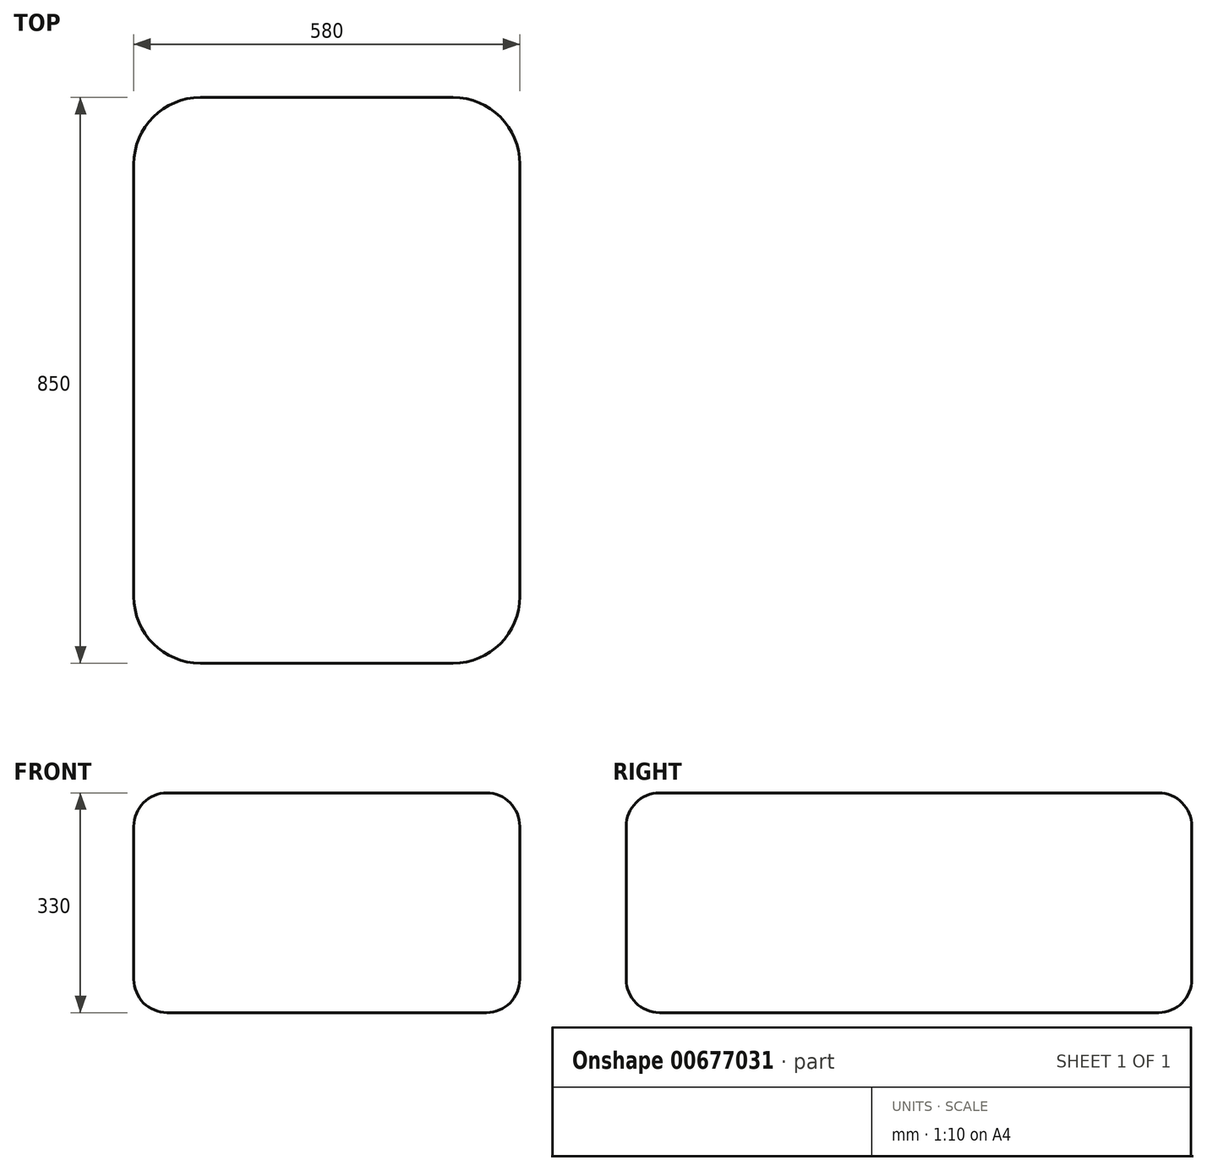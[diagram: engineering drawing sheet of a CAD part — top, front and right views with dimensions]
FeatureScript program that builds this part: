
annotation { "Feature Type Name" : "Feature", "Feature Type Description" : "" }
export const myFeature = defineFeature(function(context is Context, id is Id, definition is map)
    precondition{}
    {
        {
            var Q0;
            Q0=qCreatedBy(makeId("Top.planeOp"),FACE);
            var sketch = newSketch(context, id + "F0", { "sketchPlane" : qUnion([Q0])});
            skLineSegment(sketch, "E0.bottom", {"start": v(0, 0) * mm, "end": v(580, 0) * mm});
            skLineSegment(sketch, "E0.top", {"start": v(0, -850) * mm, "end": v(580, -850) * mm});
            skLineSegment(sketch, "E0.left", {"start": v(0, 0) * mm, "end": v(0, -850) * mm});
            skLineSegment(sketch, "E0.right", {"start": v(580, 0) * mm, "end": v(580, -850) * mm});
            skSolve(sketch);
        }
        {
            var Q0;
            Q0 = qSketchRegion(id + "F0", true);
            extrude(context, id + "F1", {"entities" : qUnion([Q0]), "depth" : 330 * mm, "offsetDistance" : 25 * mm});
        }
        {
            var Q0;
            Q0=makeQuery(id+"F1.opExtrude","SWEPT_EDGE",EDGE,{"disambiguationData":[OSD([sQuery(id+"F0.wireOp",EDGE,"E0.top"),sQuery(id+"F0.wireOp",EDGE,"E0.right")])]});
            var Q1;
            Q1=makeQuery(id+"F1.opExtrude","SWEPT_EDGE",EDGE,{"disambiguationData":[OSD([sQuery(id+"F0.wireOp",EDGE,"E0.bottom"),sQuery(id+"F0.wireOp",EDGE,"E0.right")])]});
            var Q2;
            Q2=makeQuery(id+"F1.opExtrude","SWEPT_EDGE",EDGE,{"disambiguationData":[OSD([sQuery(id+"F0.wireOp",EDGE,"E0.top"),sQuery(id+"F0.wireOp",EDGE,"E0.left")])]});
            var Q3;
            Q3=makeQuery(id+"F1.opExtrude","SWEPT_EDGE",EDGE,{"disambiguationData":[OSD([sQuery(id+"F0.wireOp",EDGE,"E0.bottom"),sQuery(id+"F0.wireOp",EDGE,"E0.left")])]});
            fillet(context, id + "F2", {"entities" : qUnion([Q0, Q1, Q2, Q3]), "radius" : 100 * mm, "tangentPropagation" : true, "allowEdgeOverflow" : false});
        }
        {
            var Q0;
            Q0=makeQuery(id+"F1.opExtrude","CAP_FACE",FACE,{"disambiguationData":[OSD([sQuery(id+"F0.wireOp",EDGE,"E0.bottom"),sQuery(id+"F0.wireOp",EDGE,"E0.top"),sQuery(id+"F0.wireOp",EDGE,"E0.left"),sQuery(id+"F0.wireOp",EDGE,"E0.right")])],"isStart":false});
            var Q1;
            Q1=makeQuery(id+"F1.opExtrude","CAP_FACE",FACE,{"disambiguationData":[OSD([sQuery(id+"F0.wireOp",EDGE,"E0.bottom"),sQuery(id+"F0.wireOp",EDGE,"E0.top"),sQuery(id+"F0.wireOp",EDGE,"E0.left"),sQuery(id+"F0.wireOp",EDGE,"E0.right")])],"isStart":true});
            fillet(context, id + "F3", {"entities" : qUnion([Q0, Q1]), "radius" : 50 * mm, "tangentPropagation" : true, "allowEdgeOverflow" : false});
        }
    });
